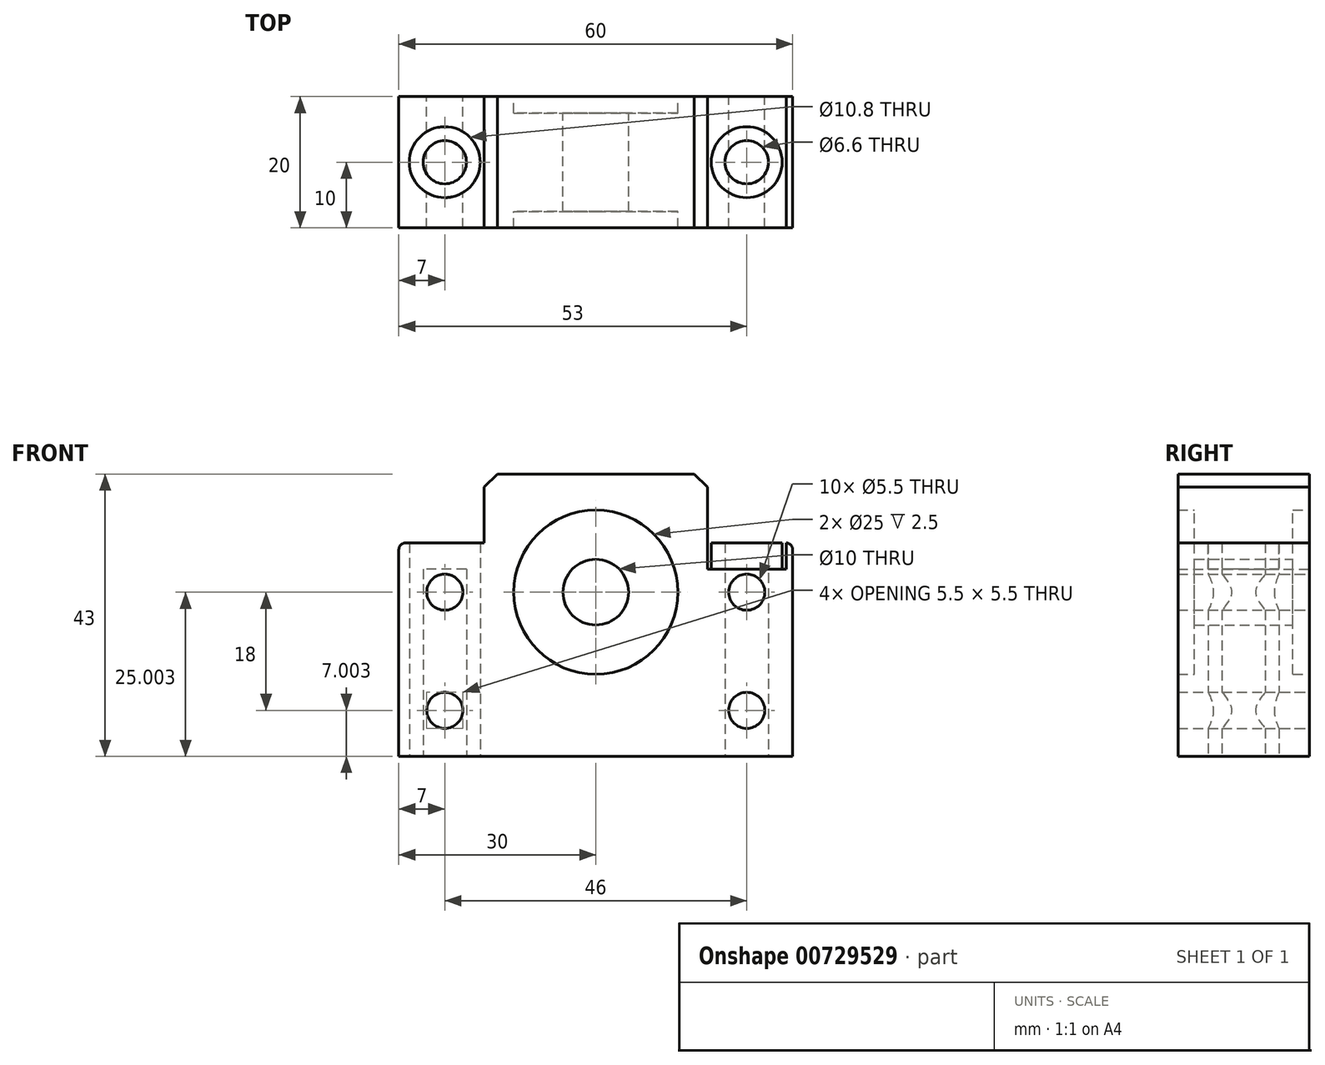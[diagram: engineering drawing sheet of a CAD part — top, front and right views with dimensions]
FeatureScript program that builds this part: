
annotation { "Feature Type Name" : "Feature", "Feature Type Description" : "" }
export const myFeature = defineFeature(function(context is Context, id is Id, definition is map)
    precondition{}
    {
        {
            var Q0;
            Q0=qCreatedBy(makeId("Front.planeOp"),FACE);
            var sketch = newSketch(context, id + "F0", { "sketchPlane" : qUnion([Q0])});
            skLineSegment(sketch, "E0", {"start": v(0, 62.09) * mm, "end": v(0, -50.94) * mm, "construction": true});
            skLineSegment(sketch, "E1.bottom", {"start": v(-30, 25.6) * mm, "end": v(-17, 25.6) * mm});
            skLineSegment(sketch, "E1.top", {"start": v(-30, -6.9) * mm, "end": v(30, -6.9) * mm});
            skLineSegment(sketch, "E1.left", {"start": v(-30, 25.6) * mm, "end": v(-30, -6.9) * mm});
            skLineSegment(sketch, "E1.right", {"start": v(30, 25.6) * mm, "end": v(30, -6.9) * mm});
            skLineSegment(sketch, "E2.top", {"start": v(-17, 36.1) * mm, "end": v(17, 36.1) * mm});
            skLineSegment(sketch, "E2.left", {"start": v(-17, 25.6) * mm, "end": v(-17, 36.1) * mm});
            skLineSegment(sketch, "E2.right", {"start": v(17, 25.6) * mm, "end": v(17, 36.1) * mm});
            skCircle(sketch, "E3", {"center": v(0, 18.1) * mm, "radius": 12.5 * mm});
            skCircle(sketch, "E4", {"center": v(0, 18.1) * mm, "radius": 5 * mm});
            skLineSegment(sketch, "E5", {"start": v(0, 18.1) * mm, "end": v(56.63, 18.1) * mm, "construction": true});
            skLineSegment(sketch, "E6", {"start": v(23, 31.07) * mm, "end": v(23, -27.42) * mm, "construction": true});
            skLineSegment(sketch, "E7.trimOffspring", {"start": v(17, 25.6) * mm, "end": v(30, 25.6) * mm});
            skLineSegment(sketch, "E8.MirrorCS", {"start": v(-23, 31.07) * mm, "end": v(-23, -27.42) * mm, "construction": true});
            skCircle(sketch, "E9", {"center": v(23, 18.1) * mm, "radius": 2.75 * mm});
            skCircle(sketch, "E10", {"center": v(23, 0.1) * mm, "radius": 2.75 * mm});
            skCircle(sketch, "E11.MirrorC", {"center": v(-23, 18.1) * mm, "radius": 2.75 * mm});
            skCircle(sketch, "E12.MirrorC", {"center": v(-23, 0.1) * mm, "radius": 2.75 * mm});
            skSolve(sketch);
        }
        {
            var Q0;
            Q0=makeQuery(id+"F0.imprint","IMPRINT",FACE,{"disambiguationData":[TD([[makeQuery(id+"F0.imprint","IMPRINT",EDGE,{"derivedFrom":sQuery(id+"F0.wireOp",EDGE,"E1.bottom")}),-1.0]])]});
            extrude(context, id + "F1", {"entities" : qUnion([Q0]), "depth" : 20 * mm, "offsetDistance" : 25 * mm, "symmetric" : true});
        }
        {
            var Q0;
            Q0=makeQuery(id+"F0.imprint","IMPRINT",FACE,{"disambiguationData":[TD([[makeQuery(id+"F0.imprint","IMPRINT",EDGE,{"derivedFrom":sQuery(id+"F0.wireOp",EDGE,"E3")}),1.0]])]});
            extrude(context, id + "F2", {"entities" : qUnion([Q0]), "operationType" : NewBodyOperationType.ADD, "depth" : 15 * mm, "offsetDistance" : 25 * mm, "symmetric" : true});
        }
        {
            var Q0;
            Q0=makeQuery(id+"F1.opExtrude","SWEPT_EDGE",EDGE,{"disambiguationData":[OSD([sQuery(id+"F0.wireOp",EDGE,"E2.top"),sQuery(id+"F0.wireOp",EDGE,"E2.left")])]});
            var Q1;
            Q1=makeQuery(id+"F1.opExtrude","SWEPT_EDGE",EDGE,{"disambiguationData":[OSD([sQuery(id+"F0.wireOp",EDGE,"E2.top"),sQuery(id+"F0.wireOp",EDGE,"E2.right")])]});
            chamfer(context, id + "F3", {"entities" : qUnion([Q0, Q1]), "width" : 2 * mm, "tangentPropagation" : true});
        }
        {
            var Q0;
            Q0=makeQuery(id+"F1.opExtrude","SWEPT_EDGE",EDGE,{"disambiguationData":[OSD([sQuery(id+"F0.wireOp",EDGE,"E1.bottom"),sQuery(id+"F0.wireOp",EDGE,"E1.left")])]});
            var Q1;
            Q1=makeQuery(id+"F1.opExtrude","SWEPT_EDGE",EDGE,{"disambiguationData":[OSD([sQuery(id+"F0.wireOp",EDGE,"E1.right"),sQuery(id+"F0.wireOp",EDGE,"E7.trimOffspring")])]});
            fillet(context, id + "F4", {"entities" : qUnion([Q0, Q1]), "radius" : 1 * mm, "tangentPropagation" : true, "allowEdgeOverflow" : false});
        }
        {
            var Q0;
            Q0=makeQuery(id+"F1.opExtrude","SWEPT_FACE",FACE,{"disambiguationData":[OSD([sQuery(id+"F0.wireOp",EDGE,"E1.top")])]});
            var sketch = newSketch(context, id + "F5", { "sketchPlane" : qUnion([Q0])});
            skLineSegment(sketch, "E13", {"start": v(23, 6.69) * mm, "end": v(23, 0) * mm, "construction": true});
            skCircle(sketch, "E14", {"center": v(23, 0) * mm, "radius": 3.3 * mm});
            skCircle(sketch, "E15", {"center": v(23, 0) * mm, "radius": 5.4 * mm});
            skLineSegment(sketch, "E16", {"start": v(0, -32.3) * mm, "end": v(0, 0) * mm, "construction": true});
            skLineSegment(sketch, "E17.MirrorCS", {"start": v(-23, 6.69) * mm, "end": v(-23, 0) * mm, "construction": true});
            skCircle(sketch, "E18.MirrorC", {"center": v(-23, 0) * mm, "radius": 5.4 * mm});
            skCircle(sketch, "E19.MirrorC", {"center": v(-23, 0) * mm, "radius": 3.3 * mm});
            skSolve(sketch);
        }
        {
            var Q0;
            Q0=makeQuery(id+"F5.imprint","IMPRINT",FACE,{"disambiguationData":[TD([[makeQuery(id+"F5.imprint","IMPRINT",EDGE,{"derivedFrom":sQuery(id+"F5.wireOp",EDGE,"E14")}),1.0]])]});
            var Q1;
            Q1=makeQuery(id+"F5.imprint","IMPRINT",FACE,{"disambiguationData":[TD([[makeQuery(id+"F5.imprint","IMPRINT",EDGE,{"derivedFrom":sQuery(id+"F5.wireOp",EDGE,"E19.MirrorC")}),-1.0]])]});
            extrude(context, id + "F6", {"entities" : qUnion([Q0, Q1]), "operationType" : NewBodyOperationType.REMOVE, "oppositeDirection" : true, "depth" : 32.5 * mm, "offsetDistance" : 25 * mm});
        }
        {
            var Q0;
            Q0=makeQuery(id+"F1.opExtrude","SWEPT_FACE",FACE,{"disambiguationData":[OSD([sQuery(id+"F0.wireOp",EDGE,"E7.trimOffspring")])]});
            var sketch = newSketch(context, id + "F7", { "sketchPlane" : qUnion([Q0])});
            skLineSegment(sketch, "E20", {"start": v(-23, 6.69) * mm, "end": v(-23, 0) * mm, "construction": true});
            skCircle(sketch, "E21", {"center": v(-23, 0) * mm, "radius": 5.4 * mm});
            skLineSegment(sketch, "E22", {"start": v(0, 0) * mm, "end": v(0, 12.36) * mm, "construction": true});
            skLineSegment(sketch, "E23.MirrorCS", {"start": v(23, 6.69) * mm, "end": v(23, 0) * mm, "construction": true});
            skCircle(sketch, "E24.MirrorC", {"center": v(23, 0) * mm, "radius": 5.4 * mm});
            skSolve(sketch);
        }
        {
            var Q0;
            Q0=makeQuery(id+"F7.imprint","IMPRINT",FACE,{"disambiguationData":[TD([[makeQuery(id+"F7.imprint","IMPRINT",EDGE,{"derivedFrom":sQuery(id+"F7.wireOp",EDGE,"E24.MirrorC")}),-1.0]])]});
            var Q1;
            Q1=makeQuery(id+"F7.imprint","IMPRINT",FACE,{"disambiguationData":[TD([[makeQuery(id+"F7.imprint","IMPRINT",EDGE,{"derivedFrom":sQuery(id+"F7.wireOp",EDGE,"E21")}),1.0]])]});
            extrude(context, id + "F8", {"entities" : qUnion([Q0, Q1]), "operationType" : NewBodyOperationType.REMOVE, "oppositeDirection" : true, "depth" : 4 * mm, "offsetDistance" : 25 * mm});
        }
    });
